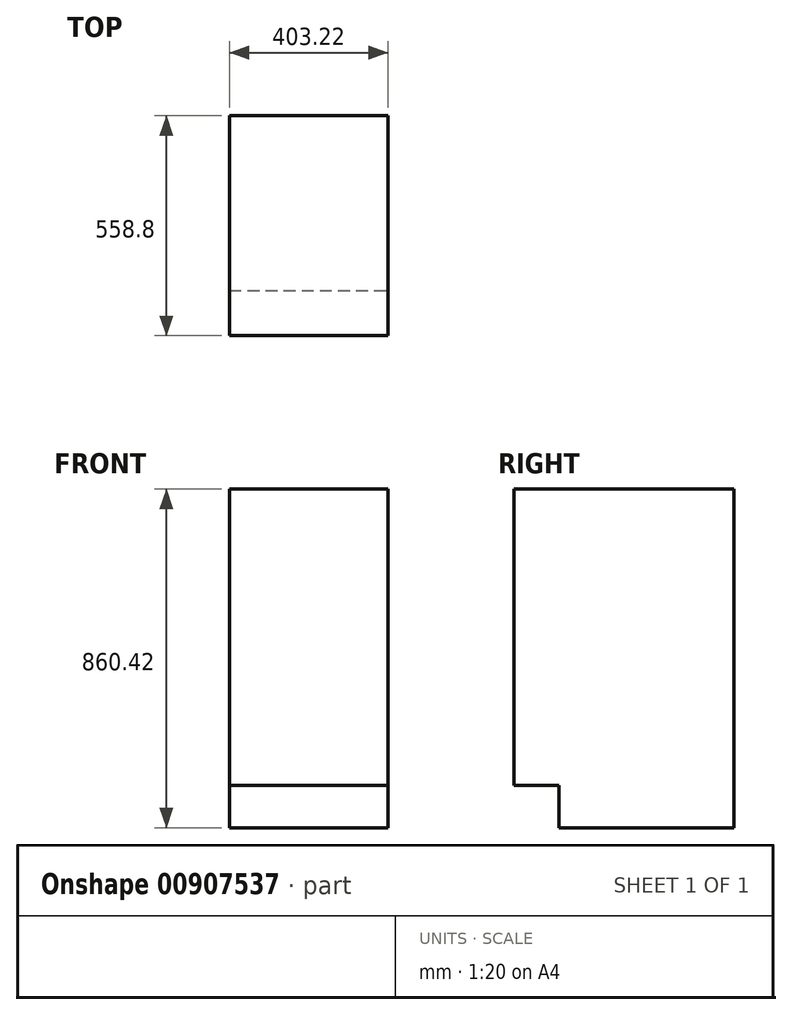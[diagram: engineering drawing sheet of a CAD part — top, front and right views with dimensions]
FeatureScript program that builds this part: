
annotation { "Feature Type Name" : "Feature", "Feature Type Description" : "" }
export const myFeature = defineFeature(function(context is Context, id is Id, definition is map)
    precondition{}
    {
        {
            var Q0;
            Q0=qCreatedBy(makeId("Front.planeOp"),FACE);
            var sketch = newSketch(context, id + "F0", { "sketchPlane" : qUnion([Q0])});
            skLineSegment(sketch, "E0.bottom", {"start": v(-188.91, 430.21) * mm, "end": v(188.91, 430.21) * mm});
            skLineSegment(sketch, "E0.top", {"start": v(-188.91, -430.21) * mm, "end": v(188.91, -430.21) * mm});
            skLineSegment(sketch, "E0.left", {"start": v(-188.91, 430.21) * mm, "end": v(-188.91, -430.21) * mm});
            skLineSegment(sketch, "E0.right", {"start": v(188.91, 430.21) * mm, "end": v(188.91, -430.21) * mm});
            skSolve(sketch);
        }
        {
            var Q0;
            Q0 = qSketchRegion(id + "F0", true);
            extrude(context, id + "F1", {"entities" : qUnion([Q0]), "depth" : 514.35 * mm, "offsetDistance" : 25.4 * mm});
        }
        {
            var Q0;
            Q0=makeQuery(id+"F1.opExtrude","SWEPT_FACE",FACE,{"disambiguationData":[OSD([sQuery(id+"F0.wireOp",EDGE,"E0.right")])]});
            extrude(context, id + "F2", {"entities" : qUnion([Q0]), "operationType" : NewBodyOperationType.ADD, "depth" : 25.4 * mm, "offsetDistance" : 25.4 * mm});
        }
        {
            var Q0;
            Q0=makeQuery(id+"F2.opExtrude","CAP_FACE",FACE,{"disambiguationData":[OSD([sQuery(id+"F0.wireOp",EDGE,"E0.right")])],"isStart":false});
            var sketch = newSketch(context, id + "F3", { "sketchPlane" : qUnion([Q0])});
            skLineSegment(sketch, "E1.bottom", {"start": v(-514.35, -322.26) * mm, "end": v(-444.5, -322.26) * mm});
            skLineSegment(sketch, "E1.top", {"start": v(-514.35, -430.21) * mm, "end": v(-444.5, -430.21) * mm});
            skLineSegment(sketch, "E1.left", {"start": v(-514.35, -322.26) * mm, "end": v(-514.35, -430.21) * mm});
            skLineSegment(sketch, "E1.right", {"start": v(-444.5, -322.26) * mm, "end": v(-444.5, -430.21) * mm});
            skSolve(sketch);
        }
        {
            var Q0;
            Q0 = qSketchRegion(id + "F3", true);
            extrude(context, id + "F4", {"entities" : qUnion([Q0]), "operationType" : NewBodyOperationType.REMOVE, "endBound" : BoundingType.THROUGH_ALL, "oppositeDirection" : true, "depth" : 25.4 * mm, "offsetDistance" : 25.4 * mm});
        }
        {
            var Q0;
            {var subQ0=sQuery(id+"F0.wireOp",EDGE,"E0.right");Q0=makeQuery(id+"F2.boolean.opBoolean","MERGE",FACE,{"derivedFrom":[makeQuery(id+"F1.opExtrude","CAP_FACE",FACE,{"disambiguationData":[OSD([sQuery(id+"F0.wireOp",EDGE,"E0.bottom"),sQuery(id+"F0.wireOp",EDGE,"E0.top"),sQuery(id+"F0.wireOp",EDGE,"E0.left"),subQ0])],"isStart":false}),makeQuery(id+"F2.opExtrude","SWEPT_FACE",FACE,{"disambiguationData":[OSD([subQ0]),TDD([makeQuery(id+"F1.opExtrude","CAP_EDGE",EDGE,{"disambiguationData":[OSD([subQ0])],"isStart":false})])]})]});}
            var sketch = newSketch(context, id + "F5", { "sketchPlane" : qUnion([Q0])});
            skLineSegment(sketch, "E2.bottom", {"start": v(-188.91, 430.21) * mm, "end": v(214.31, 430.21) * mm});
            skLineSegment(sketch, "E2.top", {"start": v(-188.91, -322.26) * mm, "end": v(214.31, -322.26) * mm});
            skLineSegment(sketch, "E2.left", {"start": v(-188.91, 430.21) * mm, "end": v(-188.91, -322.26) * mm});
            skLineSegment(sketch, "E2.right", {"start": v(214.31, 430.21) * mm, "end": v(214.31, -322.26) * mm});
            skSolve(sketch);
        }
        {
            var Q0;
            Q0 = qSketchRegion(id + "F5", true);
            extrude(context, id + "F6", {"entities" : qUnion([Q0]), "operationType" : NewBodyOperationType.ADD, "depth" : 44.45 * mm, "offsetDistance" : 25.4 * mm});
        }
    });
